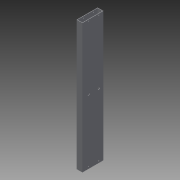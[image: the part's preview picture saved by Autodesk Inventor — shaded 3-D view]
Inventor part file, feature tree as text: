
AUTODESK INVENTOR PART (.ipt)
format: ipt  version: 2013 SP2 (Build 170200200, 200)  size: 93,696 bytes
history: native  units: mm
features: reference x4, extrude x2, sketch x2
ambient origin geometry x8: Origin, YZ Plane, XZ Plane, XY Plane, X Axis, Y Axis, Z Axis, Center Point
bodies: Solid1 (feature_tree)
feature tree (8):
  extrude  "Extrusion1"  Depth=65.0mm
  extrude  "Extrusion2"  Depth=400.0mm TaperAngle=0.0deg
  sketch  "Sketch1"  dims[d0=18.0mm d1=65.0mm]
  sketch  "Sketch2"  dims[d2=1.5mm d3=400.0mm d4=0.0mm d5=8.0mm d7=8.0mm d8=20.0mm d9=0.0mm]
  reference  "Reference1"
  reference  "Reference2"
  reference  "Reference3"
  reference  "Reference4"
